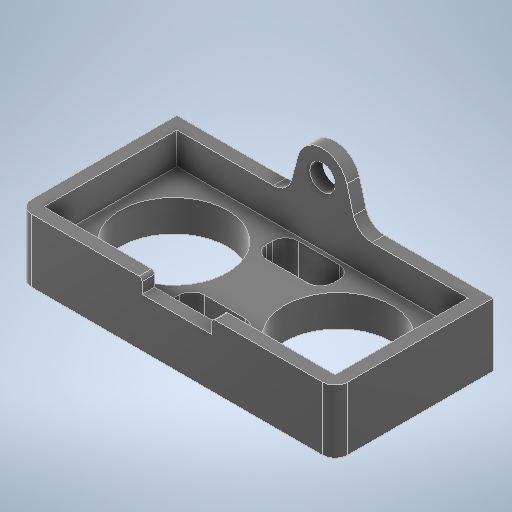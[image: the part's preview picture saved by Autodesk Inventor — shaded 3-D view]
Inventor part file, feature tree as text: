
AUTODESK INVENTOR PART (.ipt)
format: ipt  version: 2025.1 (Build 291241000, 241)  size: 367,104 bytes
history: native  units: mm
features: other x8, extrude x4, sketch x3, fillet x1
ambient origin geometry x8: Origin, YZ Plane, XZ Plane, XY Plane, X Axis, Y Axis, Z Axis, Center Point
bodies: Body1 (feature_tree)
feature tree (16):
  other  "Sólido1"
  other  "Plano de trabalho1"
  sketch  "Esboço1"  dims[d0=2.0mm d4=46.0mm]
  extrude  "Extrusão1"  Depth=46.0mm
  extrude  "Extrusão2"  Depth=21.0mm
  extrude  "Extrusão3"  Depth=0.5mm
  other  "Plano de trabalho2"
  extrude  "Extrusão5"  Depth=5.0mm TaperAngle=0.0deg
  fillet  "Arredondamento3"  Radius=5.0mm
  sketch  "Esboço2"  dims[d5=21.0mm d7=17.0mm]
  sketch  "Esboço5"  dims[d9=17.0mm d16=7.4mm d17=5.0mm d18=0.0mm d19=5.0mm d20=0.0mm d24=8.0mm d25=8.0mm d26=0.5mm d27=0.5mm d28=10.0mm d29=0.0mm d56=4.0mm d57=2.0mm d58=2.0mm d59=0.0mm d60=3.0mm d23=0.5mm]
  other  "Montagem1"
  other  "HC-SR04-UltrasonicSensor v7 v2:1"
  other  "<userpath>\Downloads\carrinho\carrinho.iam"
  other  "carrinho.iam"
  other  "base 2:1"
